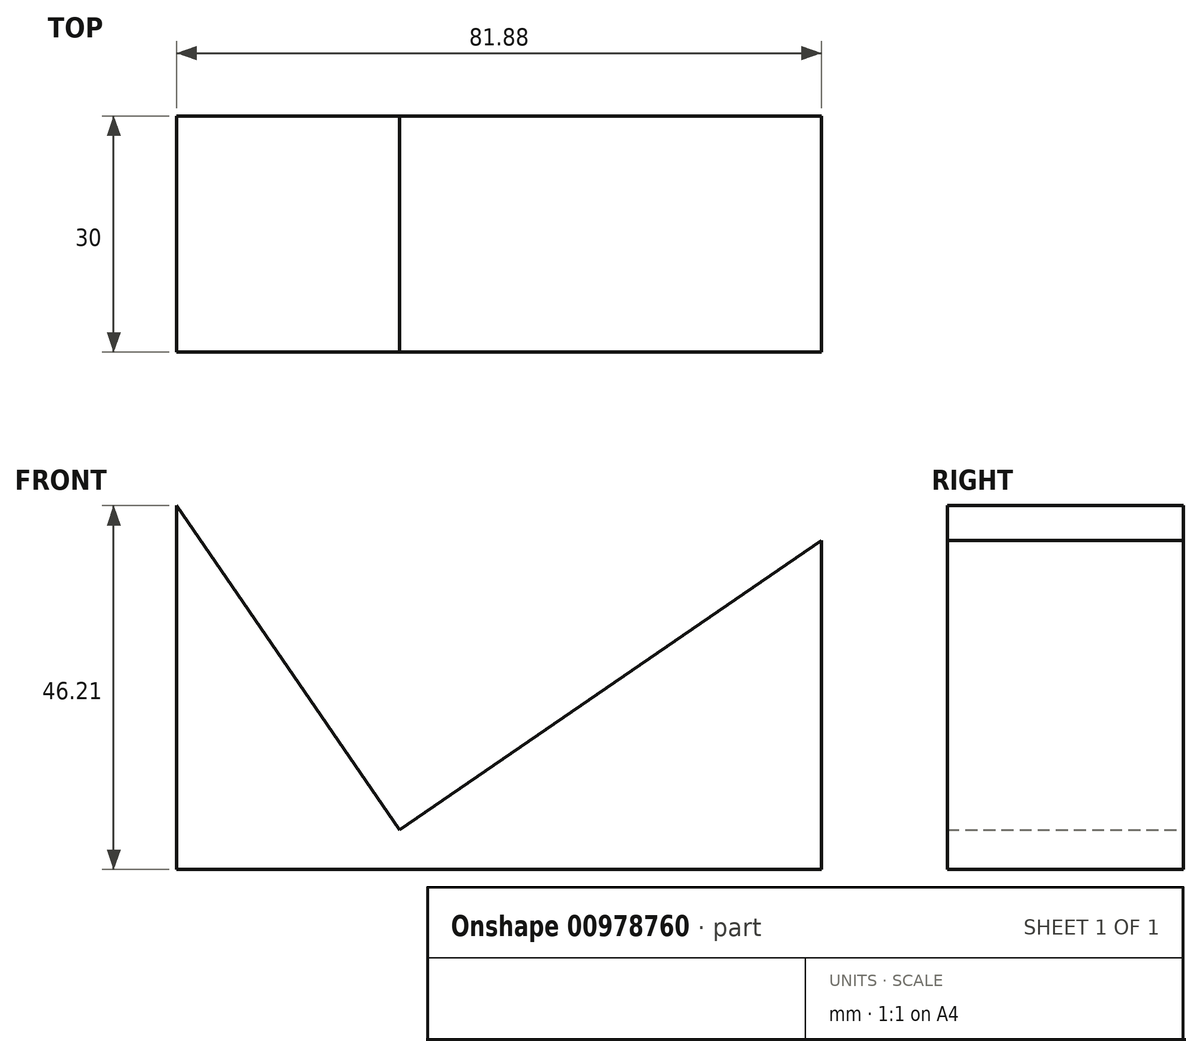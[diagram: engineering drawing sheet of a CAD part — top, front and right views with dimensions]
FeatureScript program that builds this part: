
annotation { "Feature Type Name" : "Feature", "Feature Type Description" : "" }
export const myFeature = defineFeature(function(context is Context, id is Id, definition is map)
    precondition{}
    {
        {
            var Q0;
            Q0=qCreatedBy(makeId("Front.planeOp"),FACE);
            var sketch = newSketch(context, id + "F0", { "sketchPlane" : qUnion([Q0])});
            skLineSegment(sketch, "E0", {"start": v(-40.94, 0) * mm, "end": v(-40.94, 46.2) * mm});
            skLineSegment(sketch, "E1", {"start": v(-40.94, 46.2) * mm, "end": v(-12.62, 5) * mm});
            skLineSegment(sketch, "E2", {"start": v(-12.62, 5) * mm, "end": v(40.94, 41.82) * mm});
            skLineSegment(sketch, "E3", {"start": v(40.94, 41.82) * mm, "end": v(40.94, 0) * mm});
            skLineSegment(sketch, "E4", {"start": v(40.94, 0) * mm, "end": v(-40.94, 0) * mm});
            skPoint(sketch, "E5", {"position": v(0, 0) * mm});
            skSolve(sketch);
        }
        {
            var Q0;
            Q0=makeQuery(id+"F0.imprint","IMPRINT",FACE,{"disambiguationData":[TD([[makeQuery(id+"F0.imprint","IMPRINT",EDGE,{"derivedFrom":sQuery(id+"F0.wireOp",EDGE,"E0")}),-1.0]])]});
            extrude(context, id + "F1", {"entities" : qUnion([Q0]), "endBound" : BoundingType.SYMMETRIC, "depth" : 30 * mm, "offsetDistance" : 25 * mm});
        }
    });
